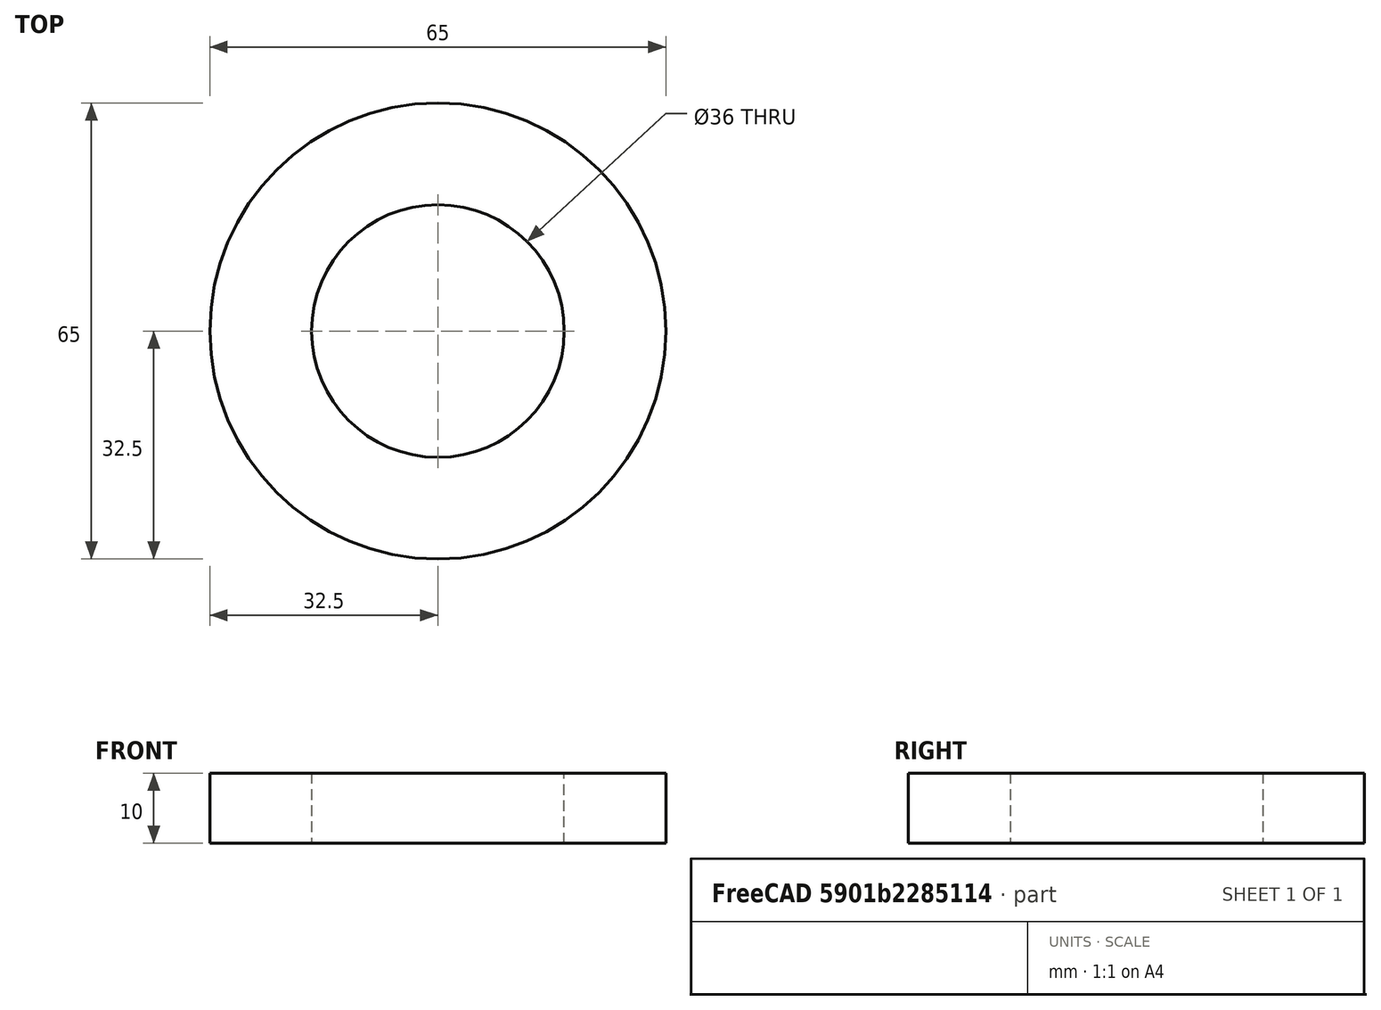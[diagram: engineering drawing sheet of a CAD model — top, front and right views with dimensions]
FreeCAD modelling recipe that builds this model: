
FCSTD DOCUMENT  (FreeCAD 0.19R24291 (Git))
Label: Hub_Flange_Cover_Back
License: All rights reserved
LicenseURL: http://en.wikipedia.org/wiki/All_rights_reserved
objects: Sketcher::SketchObject×1, PartDesign::Pad×1, PartDesign::Body×1, Spreadsheet::Sheet×1
note: 4 computed .brp shape members not serialized (recipe doc carries the construction recipe); baked Part::Feature solids carry a one-line shape summary decoded from their .brp
EXTERNAL_REF file=../../Master_of_Puppets.FCStd obj=Hub

FEATURE [Sketcher::SketchObject] Sketch
  FullyConstrained = true
  MapMode = 5
  Support = -> [XY_Plane001]
  expr: Constraints[3] = Spreadsheet.StubAxleShaftRadius
  expr: Constraints[1] = Spreadsheet.FrameSidePadRadius
  sketch-geometry (2):
    g0: Circle CenterX=0 CenterY=0 CenterZ=0 NormalX=0 NormalY=0 NormalZ=1 AngleXU=0 Radius=32.5
    g1: Circle CenterX=0 CenterY=0 CenterZ=0 NormalX=0 NormalY=0 NormalZ=1 AngleXU=0 Radius=18
  constraints (4):
    c: Coincident(g0,g-1)
    c: Radius(g0) = 32.5
    c: Coincident(g1,g-1)
    c: Radius(g1) = 18
FEATURE [PartDesign::Pad] Pad
  AllowMultiFace = false
  Direction = (1,1,1)
  Length = 10
  Length2 = 100
  Profile = -> Sketch
  Type = 0
  expr: Length = Spreadsheet.CoverThickness
FEATURE [PartDesign::Body] PadBody  label="Hub_Flange_Cover_Back"
  Group = -> [Sketch,Pad]
  Origin = -> Origin001
  Tip = -> Pad
FEATURE [Spreadsheet::Sheet] Spreadsheet
  cells = A1=Inputs; A2=CoverThickness; B2(CoverThickness)==Master_of_Puppets#Hub.CoverThickness; A3=FrameSidePadRadius; B3(FrameSidePadRadius)==Master_of_Puppets#Hub.FrameSidePadRadius; A4=StubAxleShaftRadius; B4(StubAxleShaftRadius)==Master_of_Puppets#Hub.StubAxleShaftRadius
